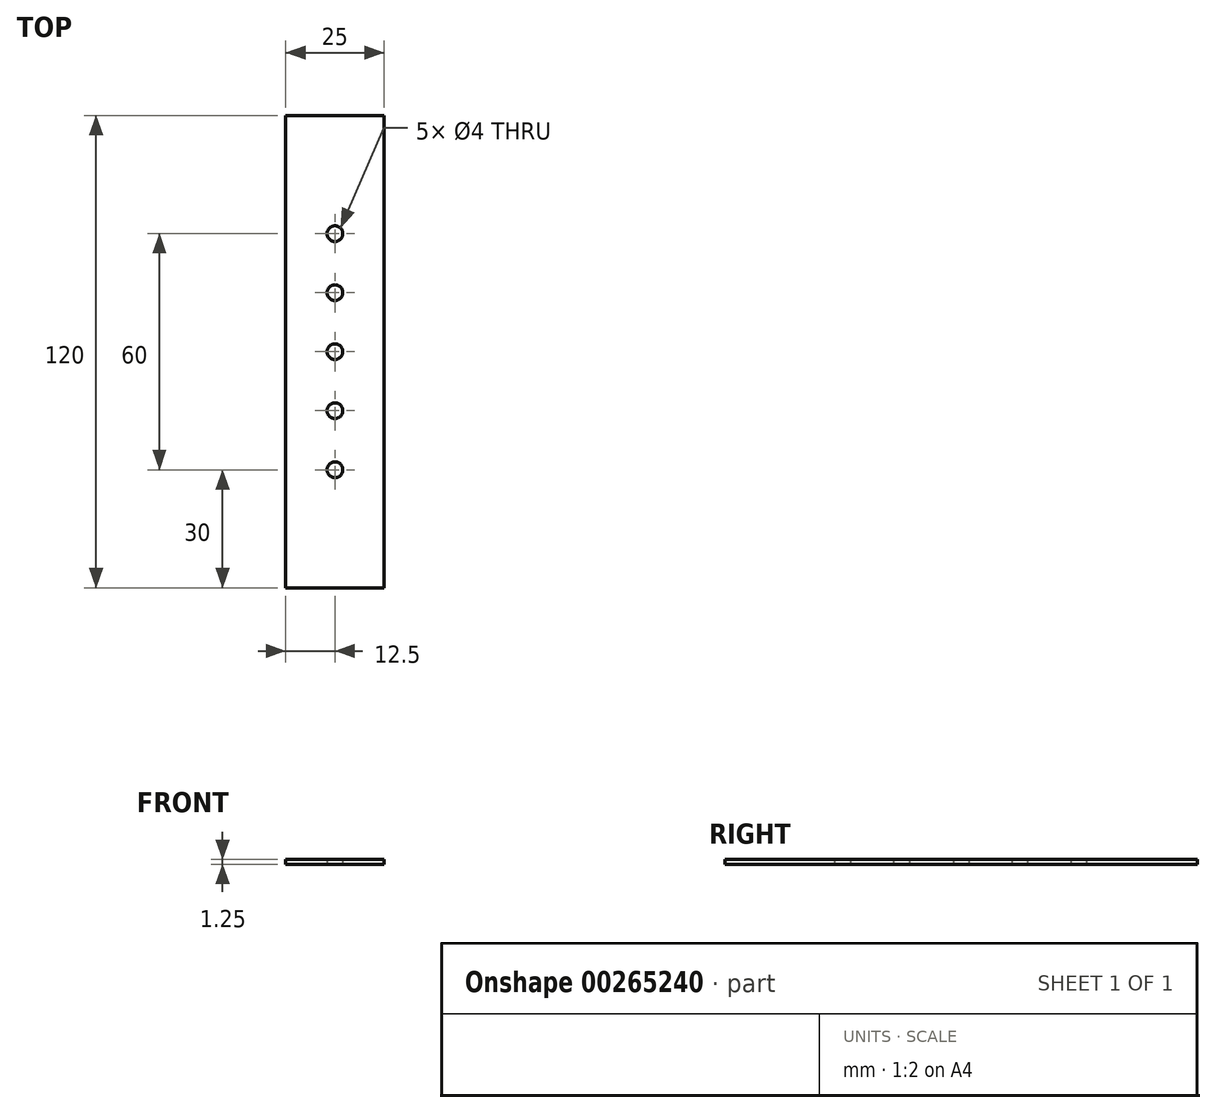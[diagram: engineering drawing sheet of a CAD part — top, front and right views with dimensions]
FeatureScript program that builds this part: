
annotation { "Feature Type Name" : "Feature", "Feature Type Description" : "" }
export const myFeature = defineFeature(function(context is Context, id is Id, definition is map)
    precondition{}
    {
        {
            var Q0;
            Q0=qCreatedBy(makeId("Top.planeOp"),FACE);
            var sketch = newSketch(context, id + "F0", { "sketchPlane" : qUnion([Q0])});
            skLineSegment(sketch, "E0.bottom", {"start": v(12.5, -60) * mm, "end": v(-12.5, -60) * mm});
            skLineSegment(sketch, "E0.top", {"start": v(12.5, 60) * mm, "end": v(-12.5, 60) * mm});
            skLineSegment(sketch, "E0.left", {"start": v(12.5, -60) * mm, "end": v(12.5, 60) * mm});
            skLineSegment(sketch, "E0.right", {"start": v(-12.5, -60) * mm, "end": v(-12.5, 60) * mm});
            skPoint(sketch, "E0.middle", {"position": v(0, 0) * mm});
            skCircle(sketch, "E1", {"center": v(0, 0) * mm, "radius": 2 * mm});
            skSolve(sketch);
        }
        {
            var Q0;
            Q0 = qSketchRegion(id + "F0", true);
            extrude(context, id + "F1", {"entities" : qUnion([Q0]), "depth" : 1.25 * mm});
        }
        {
            var Q0;
            Q0=makeQuery(id+"F1.opExtrude","CAP_FACE",FACE,{"disambiguationData":[OSD([sQuery(id+"F0.wireOp",EDGE,"E0.bottom"),sQuery(id+"F0.wireOp",EDGE,"E0.top"),sQuery(id+"F0.wireOp",EDGE,"E0.left"),sQuery(id+"F0.wireOp",EDGE,"E0.right"),sQuery(id+"F0.wireOp",EDGE,"E1")])],"isStart":false});
            var sketch = newSketch(context, id + "F2", { "sketchPlane" : qUnion([Q0])});
            skLineSegment(sketch, "E2", {"start": v(-24.96, 0) * mm, "end": v(30.57, 0) * mm, "construction": true});
            skPoint(sketch, "E2.endSnap0", {"position": v(-12.5, 0) * mm});
            skCircle(sketch, "E3", {"center": v(0, -30) * mm, "radius": 2 * mm});
            skCircle(sketch, "E4", {"center": v(0, -15) * mm, "radius": 2 * mm});
            skCircle(sketch, "E5.MirrorC", {"center": v(0, 15) * mm, "radius": 2 * mm});
            skCircle(sketch, "E6.MirrorC", {"center": v(0, 30) * mm, "radius": 2 * mm});
            skSolve(sketch);
        }
        {
            var Q0;
            Q0 = qSketchRegion(id + "F2", true);
            extrude(context, id + "F3", {"entities" : qUnion([Q0]), "operationType" : NewBodyOperationType.REMOVE, "oppositeDirection" : true, "depth" : 25 * mm});
        }
    });
